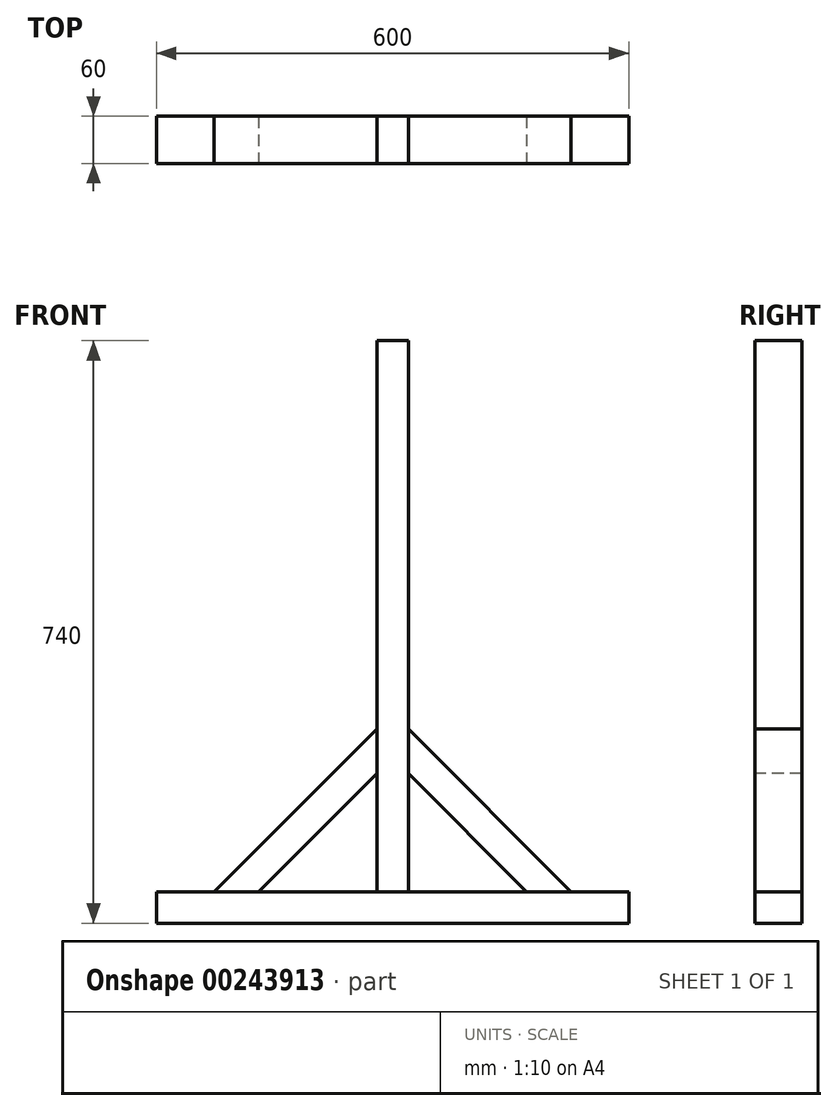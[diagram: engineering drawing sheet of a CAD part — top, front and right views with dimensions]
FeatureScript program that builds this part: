
annotation { "Feature Type Name" : "Feature", "Feature Type Description" : "" }
export const myFeature = defineFeature(function(context is Context, id is Id, definition is map)
    precondition{}
    {
        {
            var Q0;
            Q0=qCreatedBy(makeId("Top.planeOp"),FACE);
            var sketch = newSketch(context, id + "F0", { "sketchPlane" : qUnion([Q0])});
            skLineSegment(sketch, "E0.bottom", {"start": v(0, 0) * mm, "end": v(-600, 0) * mm});
            skLineSegment(sketch, "E0.top", {"start": v(0, 60) * mm, "end": v(-600, 60) * mm});
            skLineSegment(sketch, "E0.left", {"start": v(0, 0) * mm, "end": v(0, 60) * mm});
            skLineSegment(sketch, "E0.right", {"start": v(-600, 0) * mm, "end": v(-600, 60) * mm});
            skSolve(sketch);
        }
        {
            var Q0;
            Q0=makeQuery(id+"F0.imprint","IMPRINT",FACE,{"disambiguationData":[TD([[makeQuery(id+"F0.imprint","IMPRINT",EDGE,{"derivedFrom":sQuery(id+"F0.wireOp",EDGE,"E0.bottom")}),-1.0]])]});
            extrude(context, id + "F1", {"entities" : qUnion([Q0]), "depth" : 40 * mm});
        }
        {
            var Q0;
            Q0=makeQuery(id+"F1.opExtrude","CAP_FACE",FACE,{"disambiguationData":[OSD([sQuery(id+"F0.wireOp",EDGE,"E0.bottom"),sQuery(id+"F0.wireOp",EDGE,"E0.top"),sQuery(id+"F0.wireOp",EDGE,"E0.left"),sQuery(id+"F0.wireOp",EDGE,"E0.right")])],"isStart":false});
            var sketch = newSketch(context, id + "F2", { "sketchPlane" : qUnion([Q0])});
            skLineSegment(sketch, "E1", {"start": v(-300, 0) * mm, "end": v(-320, 0) * mm});
            skLineSegment(sketch, "E2", {"start": v(-320, 0) * mm, "end": v(-320, 60) * mm});
            skLineSegment(sketch, "E3", {"start": v(-320, 60) * mm, "end": v(-300, 60) * mm});
            skLineSegment(sketch, "E4", {"start": v(-300, 60) * mm, "end": v(-280, 60) * mm});
            skLineSegment(sketch, "E5", {"start": v(-280, 60) * mm, "end": v(-280, 0) * mm});
            skLineSegment(sketch, "E6", {"start": v(-280, 0) * mm, "end": v(-300, 0) * mm});
            skSolve(sketch);
        }
        {
            var Q0;
            Q0=makeQuery(id+"F2.imprint","IMPRINT",FACE,{"disambiguationData":[TD([[makeQuery(id+"F2.imprint","IMPRINT",EDGE,{"derivedFrom":sQuery(id+"F2.wireOp",EDGE,"E1")}),-1.0]])]});
            extrude(context, id + "F3", {"entities" : qUnion([Q0]), "depth" : 700 * mm});
        }
        {
            var Q0;
            Q0=makeQuery(id+"F3.opExtrude","SWEPT_FACE",FACE,{"disambiguationData":[OSD([sQuery(id+"F2.wireOp",EDGE,"E1"),sQuery(id+"F2.wireOp",EDGE,"E6")])]});
            var sketch = newSketch(context, id + "F4", { "sketchPlane" : qUnion([Q0])});
            skLineSegment(sketch, "E7", {"start": v(-320, 190) * mm, "end": v(-470, 40) * mm});
            skLineSegment(sketch, "E8", {"start": v(-470, 40) * mm, "end": v(-526.57, 40) * mm});
            skLineSegment(sketch, "E9", {"start": v(-526.57, 40) * mm, "end": v(-320, 246.57) * mm});
            skLineSegment(sketch, "E10", {"start": v(-320, 246.57) * mm, "end": v(-320, 190) * mm});
            skSolve(sketch);
        }
        {
            var Q0;
            Q0=makeQuery(id+"F4.imprint","IMPRINT",FACE,{"disambiguationData":[TD([[makeQuery(id+"F4.imprint","IMPRINT",EDGE,{"derivedFrom":sQuery(id+"F4.wireOp",EDGE,"E7")}),-1.0]])]});
            extrude(context, id + "F5", {"entities" : qUnion([Q0]), "oppositeDirection" : true, "depth" : 60 * mm});
        }
        {
            var Q0;
            Q0=makeQuery(id+"F3.opExtrude","SWEPT_FACE",FACE,{"disambiguationData":[OSD([sQuery(id+"F2.wireOp",EDGE,"E2")])]});
            cPlane(context, id + "F6", {"entities" : qUnion([Q0]), "cplaneType" : CPlaneType.OFFSET, "offset" : 20 * mm, "oppositeDirection" : true, "width" : 150 * mm, "height" : 150 * mm});
        }
        {
            var Q0;
            Q0=makeQuery(id+"F5.opExtrude","SWEPT_BODY",BODY,{"disambiguationData":[OSD([sQuery(id+"F4.wireOp",EDGE,"E7"),sQuery(id+"F4.wireOp",EDGE,"E8"),sQuery(id+"F4.wireOp",EDGE,"E9"),sQuery(id+"F4.wireOp",EDGE,"E10")])]});
            var Q1;
            Q1=qCreatedBy(id+"F6.planeOp",FACE);
            mirror(context, id + "F7", {"entities" : qUnion([Q0]), "mirrorPlane" : qUnion([Q1])});
        }
    });
